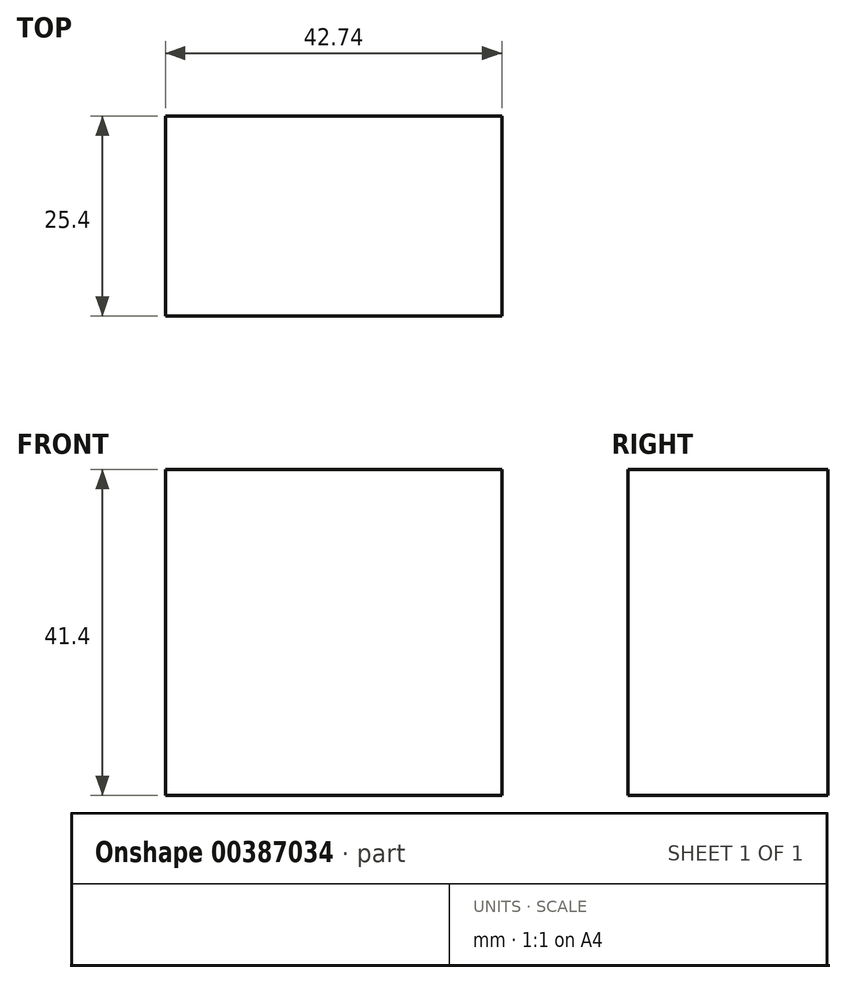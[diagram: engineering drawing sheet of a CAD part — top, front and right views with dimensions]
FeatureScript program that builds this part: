
annotation { "Feature Type Name" : "Feature", "Feature Type Description" : "" }
export const myFeature = defineFeature(function(context is Context, id is Id, definition is map)
    precondition{}
    {
        {
            var Q0;
            Q0=qCreatedBy(makeId("Front.planeOp"),FACE);
            var sketch = newSketch(context, id + "F0", { "sketchPlane" : qUnion([Q0])});
            skLineSegment(sketch, "E0.bottom", {"start": v(0, 0) * mm, "end": v(42.74, 0) * mm});
            skLineSegment(sketch, "E0.top", {"start": v(0, 41.4) * mm, "end": v(42.74, 41.4) * mm});
            skLineSegment(sketch, "E0.left", {"start": v(0, 0) * mm, "end": v(0, 41.4) * mm});
            skLineSegment(sketch, "E0.right", {"start": v(42.74, 0) * mm, "end": v(42.74, 41.4) * mm});
            skSolve(sketch);
        }
        {
            var Q0;
            Q0=makeQuery(id+"F0.imprint","IMPRINT",FACE,{"disambiguationData":[TD([[makeQuery(id+"F0.imprint","IMPRINT",EDGE,{"derivedFrom":sQuery(id+"F0.wireOp",EDGE,"E0.bottom")}),1.0]])]});
            extrude(context, id + "F1", {"entities" : qUnion([Q0]), "depth" : 25.4 * mm});
        }
    });
